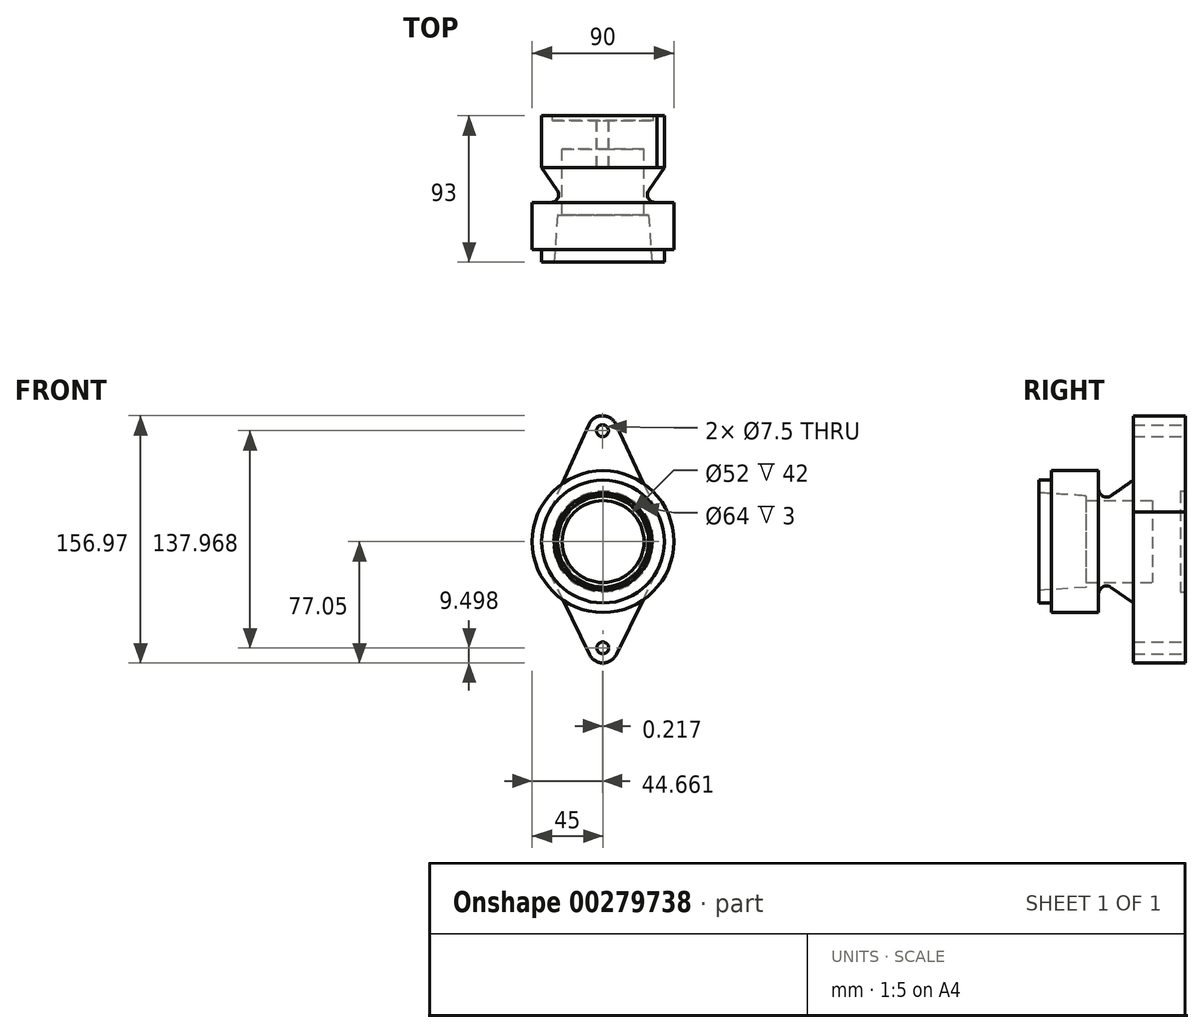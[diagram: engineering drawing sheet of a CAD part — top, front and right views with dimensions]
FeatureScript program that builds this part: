
annotation { "Feature Type Name" : "Feature", "Feature Type Description" : "" }
export const myFeature = defineFeature(function(context is Context, id is Id, definition is map)
    precondition{}
    {
        {
            var Q0;
            Q0=qCreatedBy(makeId("Right.planeOp"),FACE);
            var sketch = newSketch(context, id + "F0", { "sketchPlane" : qUnion([Q0])});
            skLineSegment(sketch, "E0", {"start": v(8, 45) * mm, "end": v(38, 45) * mm});
            skLineSegment(sketch, "E1", {"start": v(38, 45) * mm, "end": v(38, 33.2) * mm});
            skLineSegment(sketch, "E2", {"start": v(45.87, 29.1) * mm, "end": v(60, 39) * mm});
            skLineSegment(sketch, "E3", {"start": v(60, 39) * mm, "end": v(93, 39) * mm});
            skLineSegment(sketch, "E4", {"start": v(93, 39) * mm, "end": v(93, 32) * mm});
            skLineSegment(sketch, "E5", {"start": v(93, 32) * mm, "end": v(90, 32) * mm});
            skLineSegment(sketch, "E6", {"start": v(90, 32) * mm, "end": v(90, 0) * mm});
            skLineSegment(sketch, "E7", {"start": v(90, 0) * mm, "end": v(72, 0) * mm});
            skArc(sketch, "E8.filletArc", {"start": v(38, 33.2) * mm, "mid": v(40.7, 28.77) * mm, "end": v(45.87, 29.1) * mm});
            skLineSegment(sketch, "E9", {"start": v(72, 0) * mm, "end": v(72, 26) * mm});
            skLineSegment(sketch, "E10", {"start": v(72, 26) * mm, "end": v(30, 26) * mm});
            skLineSegment(sketch, "E11", {"start": v(30, 26) * mm, "end": v(30, 29) * mm});
            skLineSegment(sketch, "E12", {"start": v(8, 45) * mm, "end": v(8, 39) * mm});
            skLineSegment(sketch, "E13", {"start": v(8, 39) * mm, "end": v(0, 39) * mm});
            skLineSegment(sketch, "E14", {"start": v(30, 29) * mm, "end": v(0, 31) * mm});
            skLineSegment(sketch, "E15", {"start": v(0, 31) * mm, "end": v(0, 39) * mm});
            skSolve(sketch);
        }
        {
            var Q0;
            Q0=makeQuery(id+"F0.imprint","IMPRINT",FACE,{"disambiguationData":[TD([[makeQuery(id+"F0.imprint","IMPRINT",EDGE,{"derivedFrom":sQuery(id+"F0.wireOp",EDGE,"E0")}),-1.0]])]});
            var Q1;
            Q1=sQuery(id+"F0.wireOp",EDGE,"E7");
            revolve(context, id + "F1", {"entities" : qUnion([Q0]), "axis" : qUnion([Q1]), "revolveType" : RevolveType.FULL});
        }
        {
            var Q0;
            Q0=makeQuery(id+"F1.opRevolve","SWEPT_FACE",FACE,{"disambiguationData":[OSD([sQuery(id+"F0.wireOp",EDGE,"E4")])]});
            var sketch = newSketch(context, id + "F2", { "sketchPlane" : qUnion([Q0])});
            skCircle(sketch, "E16", {"center": v(0.34, 70.42) * mm, "radius": 3.75 * mm});
            skCircle(sketch, "E17", {"center": v(0.12, -67.55) * mm, "radius": 3.75 * mm});
            skArc(sketch, "E18", {"start": v(-8.42, -71.72) * mm, "mid": v(0.14, -77.05) * mm, "end": v(8.68, -71.69) * mm});
            skArc(sketch, "E19", {"start": v(8.98, 74.35) * mm, "mid": v(0.38, 79.92) * mm, "end": v(-8.27, 74.42) * mm});
            skLineSegment(sketch, "E20", {"start": v(-8.27, 74.42) * mm, "end": v(-34.13, 18.87) * mm});
            skLineSegment(sketch, "E21", {"start": v(8.98, 74.35) * mm, "end": v(35.5, 16.17) * mm});
            skLineSegment(sketch, "E22", {"start": v(-8.42, -71.72) * mm, "end": v(-35.05, -17.1) * mm});
            skLineSegment(sketch, "E23", {"start": v(8.68, -71.69) * mm, "end": v(35.12, -16.97) * mm});
            skArc(sketch, "E24", {"start": v(-35.05, -17.1) * mm, "mid": v(0.07, -39) * mm, "end": v(35.12, -16.97) * mm});
            skArc(sketch, "E25.trimOffspring", {"start": v(35.5, 16.17) * mm, "mid": v(1.51, 38.97) * mm, "end": v(-34.13, 18.87) * mm});
            skSolve(sketch);
        }
        {
            var Q0;
            Q0=makeQuery(id+"F2.imprint","IMPRINT",FACE,{"disambiguationData":[TD([[makeQuery(id+"F2.imprint","IMPRINT",EDGE,{"derivedFrom":sQuery(id+"F2.wireOp",EDGE,"E16")}),-1.0]])]});
            var Q1;
            Q1=makeQuery(id+"F2.imprint","IMPRINT",FACE,{"disambiguationData":[TD([[makeQuery(id+"F2.imprint","IMPRINT",EDGE,{"derivedFrom":sQuery(id+"F2.wireOp",EDGE,"E17")}),-1.0]])]});
            extrude(context, id + "F3", {"entities" : qUnion([Q0, Q1]), "operationType" : NewBodyOperationType.ADD, "oppositeDirection" : true, "depth" : 33 * mm});
        }
    });
